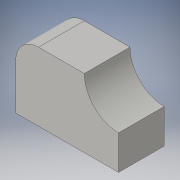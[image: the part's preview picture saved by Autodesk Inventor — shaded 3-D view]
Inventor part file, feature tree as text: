
AUTODESK INVENTOR PART (.ipt)
format: ipt  version: 2016 (Build 200138000, 138)  size: 101,376 bytes
history: native  units: in
note: dims shown in document units (in); Inventor stores cm internally (conversion verified against a paired STEP export)
features: extrude x2, sketch x2, fillet x1
ambient origin geometry x8: Origin, YZ Plane, XZ Plane, XY Plane, X Axis, Y Axis, Z Axis, Center Point
bodies: Solid1 (feature_tree)
feature tree (5):
  extrude  "Extrusion1"  Depth=1.5in
  fillet  "Fillet1"  Radius=1.0in
  extrude  "Extrusion2"  Depth=1.5in
  sketch  "Sketch1"  dims[d0=2.25in d1=1.5in d2=1.0in d3=0.0in]
  sketch  "Sketch2"  dims[d4=0.5in d5=1.5in d6=1.0in d7=0.0in]
